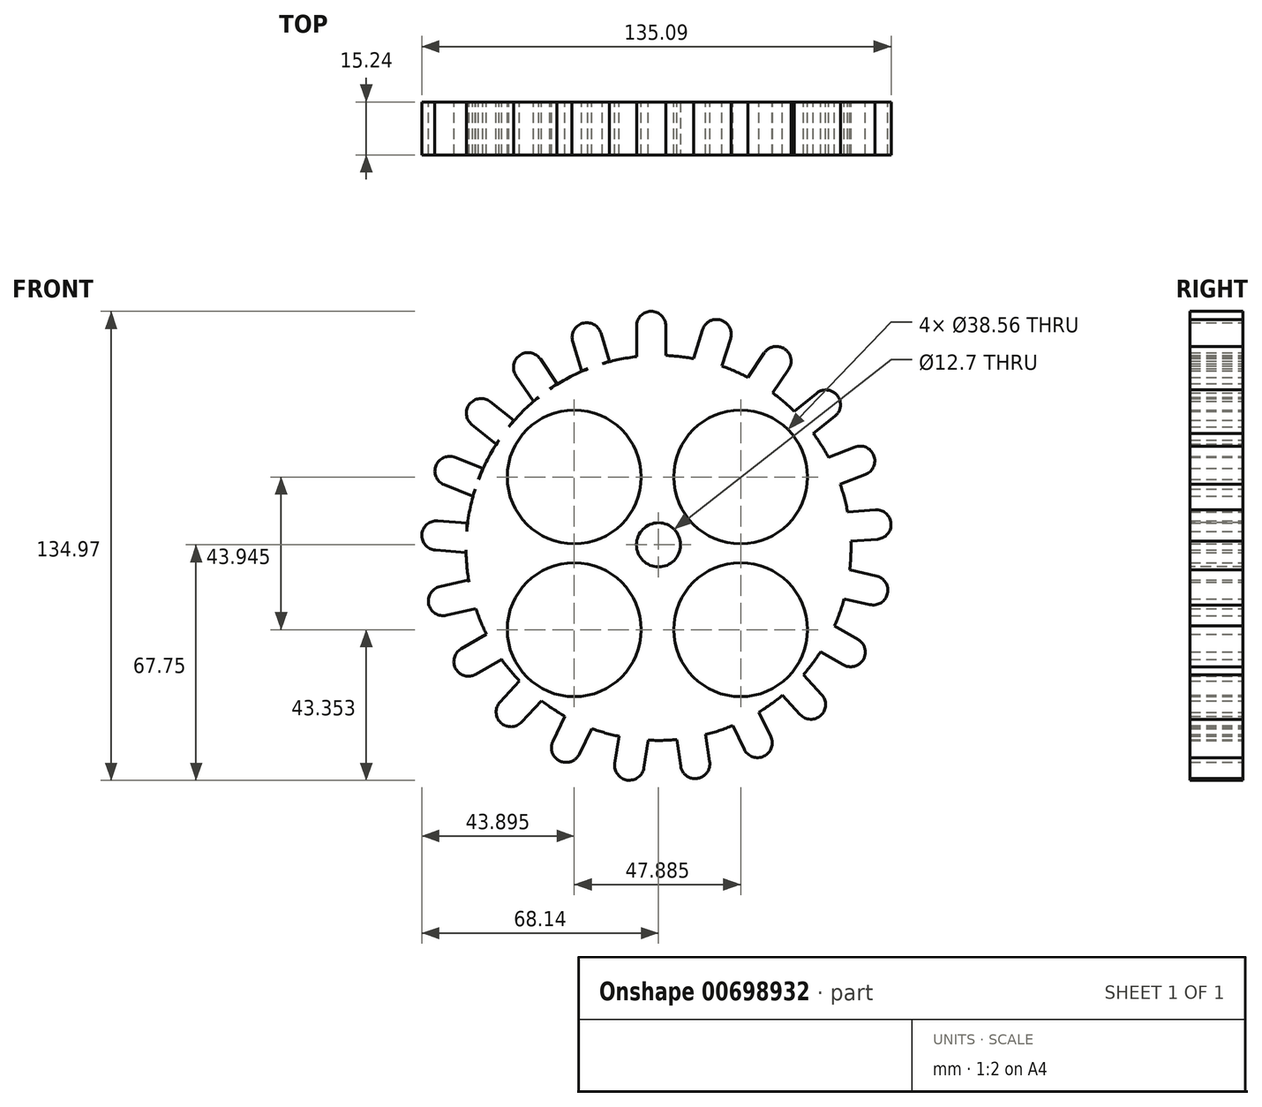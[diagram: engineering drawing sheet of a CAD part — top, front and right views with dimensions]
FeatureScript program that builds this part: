
annotation { "Feature Type Name" : "Feature", "Feature Type Description" : "" }
export const myFeature = defineFeature(function(context is Context, id is Id, definition is map)
    precondition{}
    {
        {
            var Q0;
            Q0=qCreatedBy(makeId("Front.planeOp"),FACE);
            var sketch = newSketch(context, id + "F0", { "sketchPlane" : qUnion([Q0])});
            skCircle(sketch, "E0", {"center": v(0, -0.88) * mm, "radius": 55.41 * mm});
            skCircle(sketch, "E1", {"center": v(-24.25, 19.55) * mm, "radius": 19.28 * mm});
            skCircle(sketch, "E2", {"center": v(23.64, 19.55) * mm, "radius": 19.28 * mm});
            skCircle(sketch, "E3", {"center": v(23.64, -24.4) * mm, "radius": 19.28 * mm});
            skCircle(sketch, "E4", {"center": v(-24.25, -24.4) * mm, "radius": 19.28 * mm});
            skLineSegment(sketch, "E5", {"start": v(-6.33, 54.18) * mm, "end": v(-6.33, 63) * mm});
            skLineSegment(sketch, "E6", {"start": v(2.12, 63) * mm, "end": v(2.12, 54.5) * mm});
            skLineSegment(sketch, "E7", {"start": v(2.12, 54.5) * mm, "end": v(-6.33, 54.18) * mm});
            skLineSegment(sketch, "E8.1.0", {"start": v(10.05, 53.47) * mm, "end": v(12.65, 61.9) * mm});
            skLineSegment(sketch, "E8.1.2", {"start": v(20.73, 59.4) * mm, "end": v(18.22, 51.29) * mm});
            skLineSegment(sketch, "E8.1.3", {"start": v(18.22, 51.29) * mm, "end": v(10.05, 53.47) * mm});
            skLineSegment(sketch, "E8.2.0", {"start": v(25.5, 47.97) * mm, "end": v(30.46, 55.25) * mm});
            skLineSegment(sketch, "E8.2.2", {"start": v(37.44, 50.49) * mm, "end": v(32.66, 43.47) * mm});
            skLineSegment(sketch, "E8.2.3", {"start": v(32.66, 43.47) * mm, "end": v(25.5, 47.97) * mm});
            skLineSegment(sketch, "E8.3.0", {"start": v(38.63, 38.16) * mm, "end": v(45.52, 43.65) * mm});
            skLineSegment(sketch, "E8.3.2", {"start": v(50.8, 37.04) * mm, "end": v(44.15, 31.75) * mm});
            skLineSegment(sketch, "E8.3.3", {"start": v(44.15, 31.75) * mm, "end": v(38.63, 38.16) * mm});
            skLineSegment(sketch, "E8.4.0", {"start": v(48.29, 24.91) * mm, "end": v(56.5, 28.13) * mm});
            skLineSegment(sketch, "E8.4.2", {"start": v(59.58, 20.26) * mm, "end": v(51.67, 17.16) * mm});
            skLineSegment(sketch, "E8.4.3", {"start": v(51.67, 17.16) * mm, "end": v(48.29, 24.91) * mm});
            skLineSegment(sketch, "E8.5.0", {"start": v(53.61, 9.4) * mm, "end": v(62.4, 10.06) * mm});
            skLineSegment(sketch, "E8.5.2", {"start": v(63.03, 1.63) * mm, "end": v(54.56, 1) * mm});
            skLineSegment(sketch, "E8.5.3", {"start": v(54.56, 1) * mm, "end": v(53.61, 9.4) * mm});
            skLineSegment(sketch, "E8.6.0", {"start": v(54.13, -6.98) * mm, "end": v(62.72, -8.95) * mm});
            skLineSegment(sketch, "E8.6.2", {"start": v(60.84, -17.2) * mm, "end": v(52.56, -15.3) * mm});
            skLineSegment(sketch, "E8.6.3", {"start": v(52.56, -15.3) * mm, "end": v(54.13, -6.98) * mm});
            skLineSegment(sketch, "E8.7.0", {"start": v(49.79, -22.8) * mm, "end": v(57.42, -27.2) * mm});
            skLineSegment(sketch, "E8.7.2", {"start": v(53.2, -34.53) * mm, "end": v(45.84, -30.28) * mm});
            skLineSegment(sketch, "E8.7.3", {"start": v(45.84, -30.28) * mm, "end": v(49.79, -22.8) * mm});
            skLineSegment(sketch, "E8.8.0", {"start": v(40.98, -36.62) * mm, "end": v(46.97, -43.1) * mm});
            skLineSegment(sketch, "E8.8.2", {"start": v(40.77, -48.84) * mm, "end": v(35, -42.6) * mm});
            skLineSegment(sketch, "E8.8.3", {"start": v(35, -42.6) * mm, "end": v(40.98, -36.62) * mm});
            skLineSegment(sketch, "E8.9.0", {"start": v(28.49, -47.24) * mm, "end": v(32.3, -55.19) * mm});
            skLineSegment(sketch, "E8.9.2", {"start": v(24.69, -58.85) * mm, "end": v(21, -51.2) * mm});
            skLineSegment(sketch, "E8.9.3", {"start": v(21, -51.2) * mm, "end": v(28.49, -47.24) * mm});
            skLineSegment(sketch, "E8.10.0", {"start": v(13.42, -53.7) * mm, "end": v(14.73, -62.42) * mm});
            skLineSegment(sketch, "E8.10.2", {"start": v(6.37, -63.68) * mm, "end": v(5.1, -55.28) * mm});
            skLineSegment(sketch, "E8.10.3", {"start": v(5.1, -55.28) * mm, "end": v(13.42, -53.7) * mm});
            skLineSegment(sketch, "E8.11.0", {"start": v(-2.88, -55.44) * mm, "end": v(-4.2, -64.15) * mm});
            skLineSegment(sketch, "E8.11.2", {"start": v(-12.56, -62.89) * mm, "end": v(-11.3, -54.49) * mm});
            skLineSegment(sketch, "E8.11.3", {"start": v(-11.3, -54.49) * mm, "end": v(-2.88, -55.44) * mm});
            skLineSegment(sketch, "E8.12.0", {"start": v(-18.97, -52.29) * mm, "end": v(-22.8, -60.23) * mm});
            skLineSegment(sketch, "E8.12.2", {"start": v(-30.42, -56.55) * mm, "end": v(-26.73, -48.9) * mm});
            skLineSegment(sketch, "E8.12.3", {"start": v(-26.73, -48.9) * mm, "end": v(-18.97, -52.29) * mm});
            skLineSegment(sketch, "E8.13.0", {"start": v(-33.42, -44.53) * mm, "end": v(-39.42, -50.99) * mm});
            skLineSegment(sketch, "E8.13.2", {"start": v(-45.61, -45.23) * mm, "end": v(-39.83, -39.01) * mm});
            skLineSegment(sketch, "E8.13.3", {"start": v(-39.83, -39.01) * mm, "end": v(-33.42, -44.53) * mm});
            skLineSegment(sketch, "E8.14.0", {"start": v(-44.94, -32.86) * mm, "end": v(-52.58, -37.26) * mm});
            skLineSegment(sketch, "E8.14.2", {"start": v(-56.8, -29.94) * mm, "end": v(-49.43, -25.7) * mm});
            skLineSegment(sketch, "E8.14.3", {"start": v(-49.43, -25.7) * mm, "end": v(-44.94, -32.86) * mm});
            skLineSegment(sketch, "E8.15.0", {"start": v(-52.5, -18.32) * mm, "end": v(-61.1, -20.27) * mm});
            skLineSegment(sketch, "E8.15.2", {"start": v(-62.97, -12.02) * mm, "end": v(-54.69, -10.14) * mm});
            skLineSegment(sketch, "E8.15.3", {"start": v(-54.69, -10.14) * mm, "end": v(-52.5, -18.32) * mm});
            skLineSegment(sketch, "E8.16.0", {"start": v(-55.44, -2.19) * mm, "end": v(-64.23, -1.52) * mm});
            skLineSegment(sketch, "E8.16.2", {"start": v(-63.6, 6.91) * mm, "end": v(-55.12, 6.27) * mm});
            skLineSegment(sketch, "E8.16.3", {"start": v(-55.12, 6.27) * mm, "end": v(-55.44, -2.19) * mm});
            skLineSegment(sketch, "E8.17.0", {"start": v(-53.46, 14.08) * mm, "end": v(-61.7, 17.32) * mm});
            skLineSegment(sketch, "E8.17.2", {"start": v(-58.6, 25.2) * mm, "end": v(-50.66, 22.06) * mm});
            skLineSegment(sketch, "E8.17.3", {"start": v(-50.66, 22.06) * mm, "end": v(-53.46, 14.08) * mm});
            skLineSegment(sketch, "E8.18.0", {"start": v(-46.75, 29) * mm, "end": v(-53.72, 34.58) * mm});
            skLineSegment(sketch, "E8.18.2", {"start": v(-48.44, 41.18) * mm, "end": v(-41.73, 35.81) * mm});
            skLineSegment(sketch, "E8.18.3", {"start": v(-41.73, 35.81) * mm, "end": v(-46.75, 29) * mm});
            skLineSegment(sketch, "E8.19.0", {"start": v(-36.02, 41.37) * mm, "end": v(-41.01, 48.72) * mm});
            skLineSegment(sketch, "E8.19.2", {"start": v(-34.02, 53.47) * mm, "end": v(-29.2, 46.4) * mm});
            skLineSegment(sketch, "E8.19.3", {"start": v(-29.2, 46.4) * mm, "end": v(-36.02, 41.37) * mm});
            skLineSegment(sketch, "E8.20.0", {"start": v(-22.11, 50.05) * mm, "end": v(-24.7, 58.48) * mm});
            skLineSegment(sketch, "E8.20.2", {"start": v(-16.62, 60.96) * mm, "end": v(-14.12, 52.84) * mm});
            skLineSegment(sketch, "E8.20.3", {"start": v(-14.12, 52.84) * mm, "end": v(-22.11, 50.05) * mm});
            skPoint(sketch, "E8.center", {"position": v(-0.48, -0.5) * mm});
            skLineSegment(sketch, "E8.anchor1", {"start": v(-0.48, -0.5) * mm, "end": v(-6.33, 54.18) * mm, "construction": true});
            skLineSegment(sketch, "E8.anchor2", {"start": v(-0.48, -0.5) * mm, "end": v(-22.11, 50.05) * mm, "construction": true});
            skArc(sketch, "E9", {"start": v(-24.7, 58.48) * mm, "mid": v(-21.9, 63.76) * mm, "end": v(-16.62, 60.96) * mm});
            skArc(sketch, "E10", {"start": v(-6.33, 63) * mm, "mid": v(-2.1, 67.22) * mm, "end": v(2.12, 63) * mm});
            skArc(sketch, "E11", {"start": v(12.65, 61.9) * mm, "mid": v(17.93, 64.69) * mm, "end": v(20.73, 59.4) * mm});
            skArc(sketch, "E12", {"start": v(30.46, 55.25) * mm, "mid": v(36.33, 56.36) * mm, "end": v(37.44, 50.49) * mm});
            skArc(sketch, "E13", {"start": v(45.52, 43.65) * mm, "mid": v(51.46, 42.98) * mm, "end": v(50.8, 37.04) * mm});
            skArc(sketch, "E14", {"start": v(56.5, 28.13) * mm, "mid": v(61.97, 25.74) * mm, "end": v(59.58, 20.26) * mm});
            skArc(sketch, "E15", {"start": v(62.4, 10.06) * mm, "mid": v(66.93, 6.16) * mm, "end": v(63.03, 1.63) * mm});
            skArc(sketch, "E16", {"start": v(62.72, -8.95) * mm, "mid": v(65.9, -14.01) * mm, "end": v(60.84, -17.2) * mm});
            skArc(sketch, "E17", {"start": v(57.42, -27.2) * mm, "mid": v(58.97, -32.98) * mm, "end": v(53.2, -34.53) * mm});
            skArc(sketch, "E18", {"start": v(46.97, -43.1) * mm, "mid": v(46.75, -49.06) * mm, "end": v(40.77, -48.84) * mm});
            skArc(sketch, "E19", {"start": v(32.3, -55.19) * mm, "mid": v(30.33, -60.83) * mm, "end": v(24.69, -58.85) * mm});
            skArc(sketch, "E20", {"start": v(14.73, -62.42) * mm, "mid": v(11.17, -67.23) * mm, "end": v(6.37, -63.68) * mm});
            skArc(sketch, "E21", {"start": v(-4.2, -64.15) * mm, "mid": v(-9.02, -67.7) * mm, "end": v(-12.56, -62.89) * mm});
            skArc(sketch, "E22", {"start": v(-22.8, -60.23) * mm, "mid": v(-28.45, -62.2) * mm, "end": v(-30.42, -56.55) * mm});
            skArc(sketch, "E23", {"start": v(-39.42, -50.99) * mm, "mid": v(-45.4, -51.2) * mm, "end": v(-45.61, -45.23) * mm});
            skArc(sketch, "E24", {"start": v(-52.58, -37.26) * mm, "mid": v(-58.35, -35.7) * mm, "end": v(-56.8, -29.94) * mm});
            skArc(sketch, "E25", {"start": v(-61.1, -20.27) * mm, "mid": v(-66.16, -17.08) * mm, "end": v(-62.97, -12.02) * mm});
            skArc(sketch, "E26", {"start": v(-64.23, -1.52) * mm, "mid": v(-68.13, 3.02) * mm, "end": v(-63.6, 6.91) * mm});
            skArc(sketch, "E27", {"start": v(-61.7, 17.32) * mm, "mid": v(-64.08, 22.8) * mm, "end": v(-58.6, 25.2) * mm});
            skArc(sketch, "E28", {"start": v(-53.72, 34.58) * mm, "mid": v(-54.38, 40.52) * mm, "end": v(-48.44, 41.18) * mm});
            skArc(sketch, "E29", {"start": v(-41.01, 48.72) * mm, "mid": v(-39.9, 54.6) * mm, "end": v(-34.02, 53.47) * mm});
            skSolve(sketch);
        }
        {
            var Q0;
            Q0 = qSketchRegion(id + "F0", true);
            extrude(context, id + "F1", {"entities" : qUnion([Q0]), "depth" : 15.24 * mm, "offsetDistance" : 25.4 * mm});
        }
        {
            var Q0;
            Q0=makeQuery(id+"F1.opExtrude","CAP_FACE",FACE,{"disambiguationData":[OSD([sQuery(id+"F0.wireOp",EDGE,"E0"),sQuery(id+"F0.wireOp",EDGE,"E1"),sQuery(id+"F0.wireOp",EDGE,"E2"),sQuery(id+"F0.wireOp",EDGE,"E3"),sQuery(id+"F0.wireOp",EDGE,"E4"),sQuery(id+"F0.wireOp",EDGE,"E5"),sQuery(id+"F0.wireOp",EDGE,"mib4tLzw-aGEk-I4GJ-FQfF-5oJIfVk0mLvE"),sQuery(id+"F0.wireOp",EDGE,"E6"),sQuery(id+"F0.wireOp",EDGE,"E8.1.0"),sQuery(id+"F0.wireOp",EDGE,"E8.1.1"),sQuery(id+"F0.wireOp",EDGE,"E8.1.2"),sQuery(id+"F0.wireOp",EDGE,"E8.2.0"),sQuery(id+"F0.wireOp",EDGE,"E8.2.1"),sQuery(id+"F0.wireOp",EDGE,"E8.2.2"),sQuery(id+"F0.wireOp",EDGE,"E8.3.0"),sQuery(id+"F0.wireOp",EDGE,"E8.3.1"),sQuery(id+"F0.wireOp",EDGE,"E8.3.2"),sQuery(id+"F0.wireOp",EDGE,"E8.4.0"),sQuery(id+"F0.wireOp",EDGE,"E8.4.1"),sQuery(id+"F0.wireOp",EDGE,"E8.4.2"),sQuery(id+"F0.wireOp",EDGE,"E8.5.0"),sQuery(id+"F0.wireOp",EDGE,"E8.5.1"),sQuery(id+"F0.wireOp",EDGE,"E8.5.2"),sQuery(id+"F0.wireOp",EDGE,"E8.6.0"),sQuery(id+"F0.wireOp",EDGE,"E8.6.1"),sQuery(id+"F0.wireOp",EDGE,"E8.6.2"),sQuery(id+"F0.wireOp",EDGE,"E8.7.0"),sQuery(id+"F0.wireOp",EDGE,"E8.7.1"),sQuery(id+"F0.wireOp",EDGE,"E8.7.2"),sQuery(id+"F0.wireOp",EDGE,"E8.8.0"),sQuery(id+"F0.wireOp",EDGE,"E8.8.1"),sQuery(id+"F0.wireOp",EDGE,"E8.8.2"),sQuery(id+"F0.wireOp",EDGE,"E8.9.0"),sQuery(id+"F0.wireOp",EDGE,"E8.9.1"),sQuery(id+"F0.wireOp",EDGE,"E8.9.2"),sQuery(id+"F0.wireOp",EDGE,"E8.10.0"),sQuery(id+"F0.wireOp",EDGE,"E8.10.1"),sQuery(id+"F0.wireOp",EDGE,"E8.10.2"),sQuery(id+"F0.wireOp",EDGE,"E8.11.0"),sQuery(id+"F0.wireOp",EDGE,"E8.11.1"),sQuery(id+"F0.wireOp",EDGE,"E8.11.2"),sQuery(id+"F0.wireOp",EDGE,"E8.12.0"),sQuery(id+"F0.wireOp",EDGE,"E8.12.1"),sQuery(id+"F0.wireOp",EDGE,"E8.12.2"),sQuery(id+"F0.wireOp",EDGE,"E8.13.0"),sQuery(id+"F0.wireOp",EDGE,"E8.13.1"),sQuery(id+"F0.wireOp",EDGE,"E8.13.2"),sQuery(id+"F0.wireOp",EDGE,"E8.14.0"),sQuery(id+"F0.wireOp",EDGE,"E8.14.1"),sQuery(id+"F0.wireOp",EDGE,"E8.14.2"),sQuery(id+"F0.wireOp",EDGE,"E8.15.0"),sQuery(id+"F0.wireOp",EDGE,"E8.15.1"),sQuery(id+"F0.wireOp",EDGE,"E8.15.2"),sQuery(id+"F0.wireOp",EDGE,"E8.16.0"),sQuery(id+"F0.wireOp",EDGE,"E8.16.1"),sQuery(id+"F0.wireOp",EDGE,"E8.16.2"),sQuery(id+"F0.wireOp",EDGE,"E8.17.0"),sQuery(id+"F0.wireOp",EDGE,"E8.17.1"),sQuery(id+"F0.wireOp",EDGE,"E8.17.2"),sQuery(id+"F0.wireOp",EDGE,"E8.18.0"),sQuery(id+"F0.wireOp",EDGE,"E8.18.1"),sQuery(id+"F0.wireOp",EDGE,"E8.18.2"),sQuery(id+"F0.wireOp",EDGE,"E8.19.0"),sQuery(id+"F0.wireOp",EDGE,"E8.19.1"),sQuery(id+"F0.wireOp",EDGE,"E8.19.2"),sQuery(id+"F0.wireOp",EDGE,"E8.20.0"),sQuery(id+"F0.wireOp",EDGE,"E8.20.1"),sQuery(id+"F0.wireOp",EDGE,"E8.20.2")])],"isStart":false});
            var sketch = newSketch(context, id + "F2", { "sketchPlane" : qUnion([Q0])});
            skCircle(sketch, "E30", {"center": v(0, 0) * mm, "radius": 6.35 * mm});
            skSolve(sketch);
        }
        {
            var Q0;
            Q0 = qSketchRegion(id + "F2", true);
            extrude(context, id + "F3", {"entities" : qUnion([Q0]), "operationType" : NewBodyOperationType.REMOVE, "oppositeDirection" : true, "depth" : 25.4 * mm, "offsetDistance" : 25.4 * mm});
        }
        {
            var Q0;
            Q0 = qSketchRegion(id + "F2", true);
            extrude(context, id + "F4", {"entities" : qUnion([Q0]), "operationType" : NewBodyOperationType.REMOVE, "oppositeDirection" : true, "depth" : 25.4 * mm, "offsetDistance" : 25.4 * mm});
        }
    });
